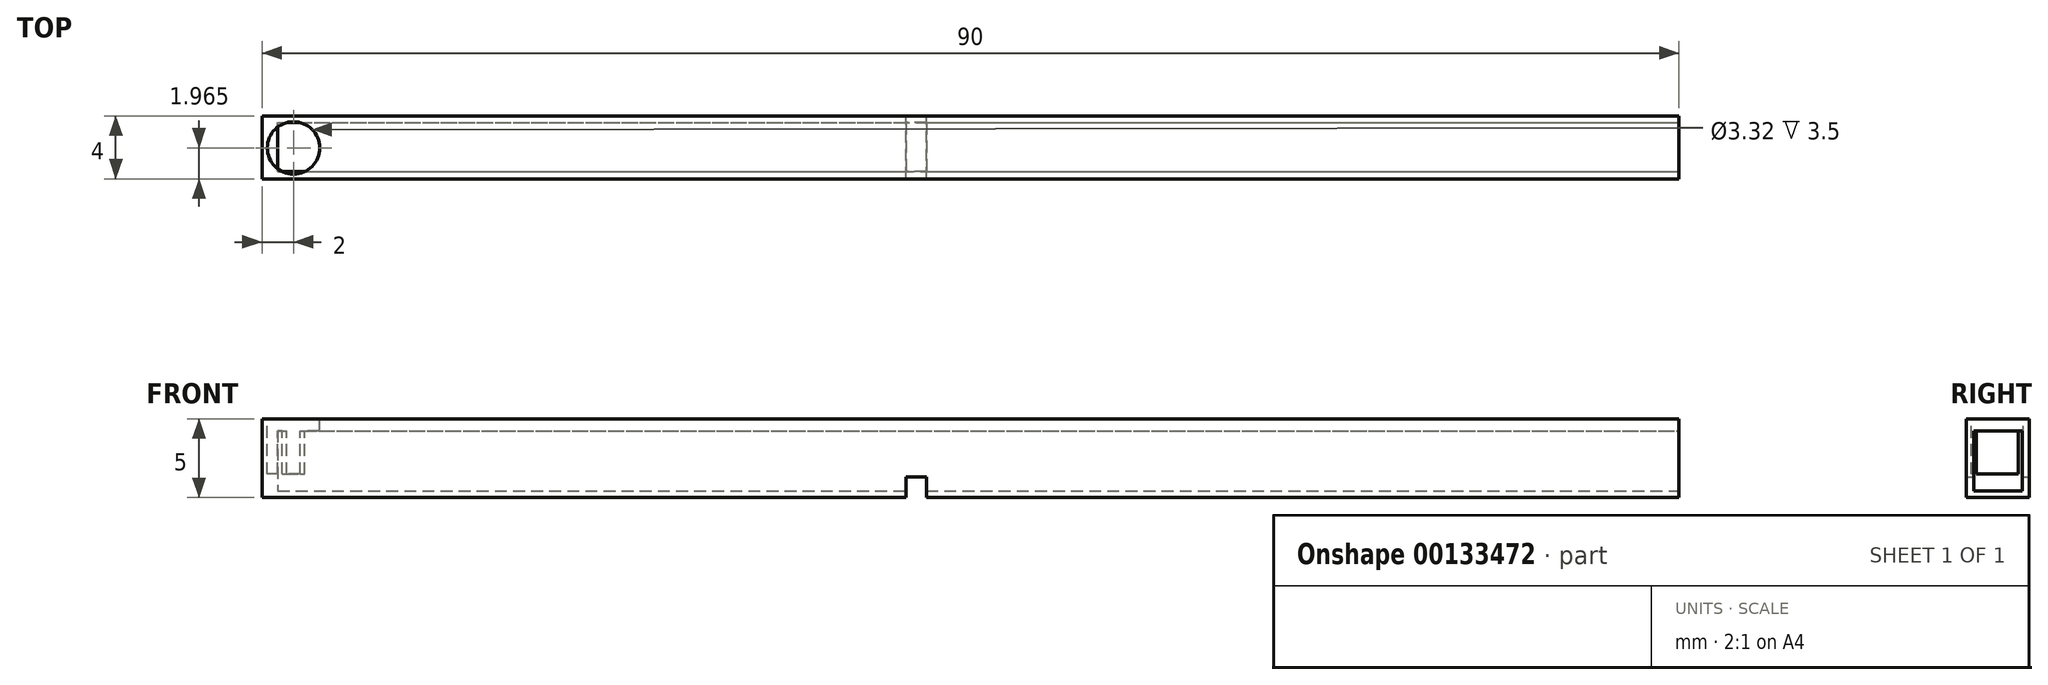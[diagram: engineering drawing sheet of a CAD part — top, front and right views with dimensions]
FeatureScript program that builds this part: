
annotation { "Feature Type Name" : "Feature", "Feature Type Description" : "" }
export const myFeature = defineFeature(function(context is Context, id is Id, definition is map)
    precondition{}
    {
        {
            var Q0;
            Q0=qCreatedBy(makeId("Top.planeOp"),FACE);
            var sketch = newSketch(context, id + "F0", { "sketchPlane" : qUnion([Q0])});
            skLineSegment(sketch, "E0.bottom", {"start": v(-35.03, 18.83) * mm, "end": v(54.97, 18.83) * mm});
            skLineSegment(sketch, "E0.top", {"start": v(-35.03, 14.83) * mm, "end": v(54.97, 14.83) * mm});
            skLineSegment(sketch, "E0.left", {"start": v(-35.03, 18.83) * mm, "end": v(-35.03, 14.83) * mm});
            skLineSegment(sketch, "E0.right", {"start": v(54.97, 18.83) * mm, "end": v(54.97, 14.83) * mm});
            skSolve(sketch);
        }
        {
            var Q0;
            Q0=makeQuery(id+"F0.imprint","IMPRINT",FACE,{"disambiguationData":[TD([[makeQuery(id+"F0.imprint","IMPRINT",EDGE,{"derivedFrom":sQuery(id+"F0.wireOp",EDGE,"E0.bottom")}),-1.0]])]});
            extrude(context, id + "F1", {"entities" : qUnion([Q0]), "depth" : 5 * mm});
        }
        {
            var Q0;
            Q0=makeQuery(id+"F1.opExtrude","CAP_FACE",FACE,{"disambiguationData":[OSD([sQuery(id+"F0.wireOp",EDGE,"E0.bottom"),sQuery(id+"F0.wireOp",EDGE,"E0.top"),sQuery(id+"F0.wireOp",EDGE,"E0.left"),sQuery(id+"F0.wireOp",EDGE,"E0.right")])],"isStart":false});
            var sketch = newSketch(context, id + "F2", { "sketchPlane" : qUnion([Q0])});
            skCircle(sketch, "E1", {"center": v(-33.03, 16.8) * mm, "radius": 1.66 * mm});
            skSolve(sketch);
        }
        {
            var Q0;
            Q0=makeQuery(id+"F2.imprint","IMPRINT",FACE,{"disambiguationData":[TD([[makeQuery(id+"F2.imprint","IMPRINT",EDGE,{"derivedFrom":sQuery(id+"F2.wireOp",EDGE,"E1")}),1.0]])]});
            extrude(context, id + "F3", {"entities" : qUnion([Q0]), "operationType" : NewBodyOperationType.REMOVE, "oppositeDirection" : true, "depth" : 3.5 * mm});
        }
        {
            var Q0;
            Q0=makeQuery(id+"F1.opExtrude","CAP_FACE",FACE,{"disambiguationData":[OSD([sQuery(id+"F0.wireOp",EDGE,"E0.bottom"),sQuery(id+"F0.wireOp",EDGE,"E0.top"),sQuery(id+"F0.wireOp",EDGE,"E0.left"),sQuery(id+"F0.wireOp",EDGE,"E0.right")])],"isStart":true});
            var sketch = newSketch(context, id + "F4", { "sketchPlane" : qUnion([Q0])});
            skCircle(sketch, "E2", {"center": v(52.59, -16.87) * mm, "radius": 0.45 * mm});
            skSolve(sketch);
        }
        {
            var Q0;
            Q0=sQuery(id+"F4.wireOp",EDGE,"E2");
            extrude(context, id + "F5", {"bodyType" : ToolBodyType.SURFACE, "surfaceEntities" : qUnion([Q0]), "depth" : 5 * mm});
        }
        {
            var Q0;
            Q0=makeQuery(id+"F1.opExtrude","CAP_FACE",FACE,{"disambiguationData":[OSD([sQuery(id+"F0.wireOp",EDGE,"E0.bottom"),sQuery(id+"F0.wireOp",EDGE,"E0.top"),sQuery(id+"F0.wireOp",EDGE,"E0.left"),sQuery(id+"F0.wireOp",EDGE,"E0.right")])],"isStart":true});
            var sketch = newSketch(context, id + "F6", { "sketchPlane" : qUnion([Q0])});
            skLineSegment(sketch, "E3.bottom", {"start": v(5.86, -14.83) * mm, "end": v(7.16, -14.83) * mm});
            skLineSegment(sketch, "E3.top", {"start": v(5.86, -18.83) * mm, "end": v(7.16, -18.83) * mm});
            skLineSegment(sketch, "E3.left", {"start": v(5.86, -14.83) * mm, "end": v(5.86, -18.83) * mm});
            skLineSegment(sketch, "E3.right", {"start": v(7.16, -14.83) * mm, "end": v(7.16, -18.83) * mm});
            skSolve(sketch);
        }
        {
            var Q0;
            Q0=makeQuery(id+"F6.imprint","IMPRINT",FACE,{"disambiguationData":[TD([[makeQuery(id+"F6.imprint","IMPRINT",EDGE,{"derivedFrom":sQuery(id+"F6.wireOp",EDGE,"E3.bottom")}),-1.0]])]});
            extrude(context, id + "F7", {"entities" : qUnion([Q0]), "operationType" : NewBodyOperationType.REMOVE, "oppositeDirection" : true, "depth" : 1.3 * mm});
        }
        {
            var Q0;
            Q0=makeQuery(id+"F1.opExtrude","SWEPT_FACE",FACE,{"disambiguationData":[OSD([sQuery(id+"F0.wireOp",EDGE,"E0.right")])]});
            var sketch = newSketch(context, id + "F8", { "sketchPlane" : qUnion([Q0])});
            skLineSegment(sketch, "E4.bottom", {"start": v(15.3, 4.25) * mm, "end": v(18.4, 4.25) * mm});
            skLineSegment(sketch, "E4.top", {"start": v(15.3, 0.41) * mm, "end": v(18.4, 0.41) * mm});
            skLineSegment(sketch, "E4.left", {"start": v(15.3, 4.25) * mm, "end": v(15.3, 0.41) * mm});
            skLineSegment(sketch, "E4.right", {"start": v(18.4, 4.25) * mm, "end": v(18.4, 0.41) * mm});
            skSolve(sketch);
        }
        {
            var Q0;
            Q0=makeQuery(id+"F8.imprint","IMPRINT",FACE,{"disambiguationData":[TD([[makeQuery(id+"F8.imprint","IMPRINT",EDGE,{"derivedFrom":sQuery(id+"F8.wireOp",EDGE,"E4.bottom")}),-1.0]])]});
            extrude(context, id + "F9", {"entities" : qUnion([Q0]), "operationType" : NewBodyOperationType.REMOVE, "oppositeDirection" : true, "depth" : 89 * mm});
        }
    });
